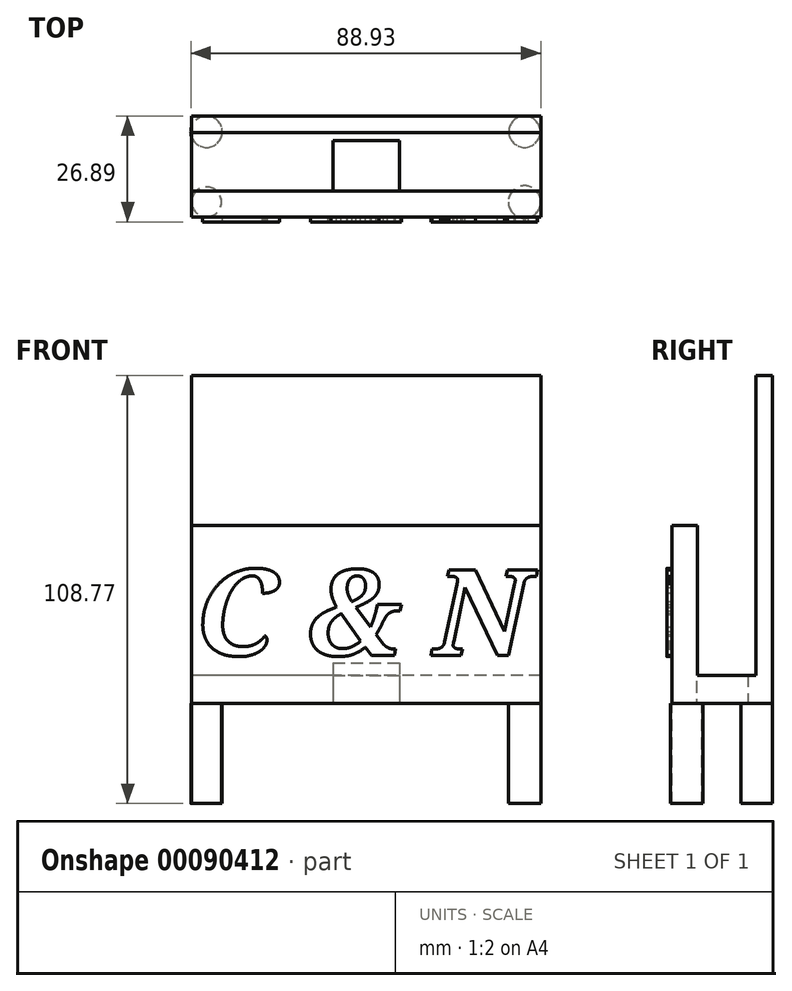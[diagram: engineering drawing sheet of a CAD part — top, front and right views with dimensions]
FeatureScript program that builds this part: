
annotation { "Feature Type Name" : "Feature", "Feature Type Description" : "" }
export const myFeature = defineFeature(function(context is Context, id is Id, definition is map)
    precondition{}
    {
        {
            var Q0;
            Q0=qCreatedBy(makeId("Top.planeOp"),FACE);
            var sketch = newSketch(context, id + "F0", { "sketchPlane" : qUnion([Q0])});
            skLineSegment(sketch, "E0.bottom", {"start": v(44.35, -12.8) * mm, "end": v(-44.35, -12.8) * mm});
            skLineSegment(sketch, "E0.top", {"start": v(44.35, 12.8) * mm, "end": v(-44.35, 12.8) * mm});
            skLineSegment(sketch, "E0.left", {"start": v(44.35, -12.8) * mm, "end": v(44.35, 12.8) * mm});
            skLineSegment(sketch, "E0.right", {"start": v(-44.35, -12.8) * mm, "end": v(-44.35, 12.8) * mm});
            skPoint(sketch, "E0.middle", {"position": v(0, 0) * mm});
            skSolve(sketch);
        }
        {
            var Q0;
            Q0 = qSketchRegion(id + "F0", true);
            extrude(context, id + "F1", {"entities" : qUnion([Q0]), "depth" : 7.17 * mm});
        }
        {
            var Q0;
            Q0=makeQuery(id+"F1.opExtrude","CAP_FACE",FACE,{"disambiguationData":[OSD([sQuery(id+"F0.wireOp",EDGE,"E0.bottom"),sQuery(id+"F0.wireOp",EDGE,"E0.top"),sQuery(id+"F0.wireOp",EDGE,"E0.left"),sQuery(id+"F0.wireOp",EDGE,"E0.right")])],"isStart":false});
            var sketch = newSketch(context, id + "F2", { "sketchPlane" : qUnion([Q0])});
            skLineSegment(sketch, "E1.bottom", {"start": v(44.35, 12.8) * mm, "end": v(-44.35, 12.8) * mm});
            skLineSegment(sketch, "E1.top", {"start": v(44.35, 8.56) * mm, "end": v(-44.35, 8.56) * mm});
            skLineSegment(sketch, "E1.left", {"start": v(44.35, 12.8) * mm, "end": v(44.35, 8.56) * mm});
            skLineSegment(sketch, "E1.right", {"start": v(-44.35, 12.8) * mm, "end": v(-44.35, 8.56) * mm});
            skSolve(sketch);
        }
        {
            var Q0;
            Q0=makeQuery(id+"F2.imprint","IMPRINT",FACE,{"disambiguationData":[TD([[makeQuery(id+"F2.imprint","IMPRINT",EDGE,{"derivedFrom":sQuery(id+"F2.wireOp",EDGE,"E1.bottom")}),1.0]])]});
            extrude(context, id + "F3", {"entities" : qUnion([Q0]), "operationType" : NewBodyOperationType.ADD, "depth" : 76.2 * mm});
        }
        {
            var Q0;
            Q0=makeQuery(id+"F1.opExtrude","CAP_FACE",FACE,{"disambiguationData":[OSD([sQuery(id+"F0.wireOp",EDGE,"E0.bottom"),sQuery(id+"F0.wireOp",EDGE,"E0.top"),sQuery(id+"F0.wireOp",EDGE,"E0.left"),sQuery(id+"F0.wireOp",EDGE,"E0.right")])],"isStart":false});
            var sketch = newSketch(context, id + "F4", { "sketchPlane" : qUnion([Q0])});
            skLineSegment(sketch, "E2.bottom", {"start": v(44.35, -12.8) * mm, "end": v(-44.35, -12.8) * mm});
            skLineSegment(sketch, "E2.top", {"start": v(44.35, -6.26) * mm, "end": v(-44.35, -6.26) * mm});
            skLineSegment(sketch, "E2.left", {"start": v(44.35, -12.8) * mm, "end": v(44.35, -6.26) * mm});
            skLineSegment(sketch, "E2.right", {"start": v(-44.35, -12.8) * mm, "end": v(-44.35, -6.26) * mm});
            skSolve(sketch);
        }
        {
            var Q0;
            Q0 = qSketchRegion(id + "F4", true);
            extrude(context, id + "F5", {"entities" : qUnion([Q0]), "operationType" : NewBodyOperationType.ADD, "depth" : 38.1 * mm});
        }
        {
            var Q0;
            Q0=makeQuery(id+"F1.opExtrude","CAP_FACE",FACE,{"disambiguationData":[OSD([sQuery(id+"F0.wireOp",EDGE,"E0.bottom"),sQuery(id+"F0.wireOp",EDGE,"E0.top"),sQuery(id+"F0.wireOp",EDGE,"E0.left"),sQuery(id+"F0.wireOp",EDGE,"E0.right")])],"isStart":true});
            var sketch = newSketch(context, id + "F6", { "sketchPlane" : qUnion([Q0])});
            skLineSegment(sketch, "E3.bottom", {"start": v(8.42, 6.55) * mm, "end": v(-8.42, 6.55) * mm});
            skLineSegment(sketch, "E3.top", {"start": v(8.42, -6.55) * mm, "end": v(-8.42, -6.55) * mm});
            skLineSegment(sketch, "E3.left", {"start": v(8.42, 6.55) * mm, "end": v(8.42, -6.55) * mm});
            skLineSegment(sketch, "E3.right", {"start": v(-8.42, 6.55) * mm, "end": v(-8.42, -6.55) * mm});
            skPoint(sketch, "E3.middle", {"position": v(0, 0) * mm});
            skSolve(sketch);
        }
        {
            var Q0;
            Q0 = qSketchRegion(id + "F6", true);
            extrude(context, id + "F7", {"entities" : qUnion([Q0]), "operationType" : NewBodyOperationType.REMOVE, "oppositeDirection" : true, "depth" : 10.35 * mm});
        }
        {
            var Q0;
            Q0=makeQuery(id+"F1.opExtrude","CAP_FACE",FACE,{"disambiguationData":[OSD([sQuery(id+"F0.wireOp",EDGE,"E0.bottom"),sQuery(id+"F0.wireOp",EDGE,"E0.top"),sQuery(id+"F0.wireOp",EDGE,"E0.left"),sQuery(id+"F0.wireOp",EDGE,"E0.right")])],"isStart":true});
            var sketch = newSketch(context, id + "F8", { "sketchPlane" : qUnion([Q0])});
            skCircle(sketch, "E4", {"center": v(40.22, 9.01) * mm, "radius": 4.13 * mm});
            skCircle(sketch, "E5", {"center": v(40.22, -8.81) * mm, "radius": 4 * mm});
            skCircle(sketch, "E6", {"center": v(-40.58, -8.81) * mm, "radius": 4 * mm});
            skCircle(sketch, "E7", {"center": v(-40.58, 9.01) * mm, "radius": 3.8 * mm});
            skSolve(sketch);
        }
        {
            var Q0;
            Q0 = qSketchRegion(id + "F8", true);
            extrude(context, id + "F9", {"entities" : qUnion([Q0]), "operationType" : NewBodyOperationType.ADD, "depth" : 25.4 * mm});
        }
        {
            var Q0;
            Q0=makeQuery(id+"F5.boolean.opBoolean","MERGE",FACE,{"derivedFrom":[makeQuery(id+"F1.opExtrude","SWEPT_FACE",FACE,{"disambiguationData":[OSD([sQuery(id+"F0.wireOp",EDGE,"E0.bottom")])]}),makeQuery(id+"F5.opExtrude","SWEPT_FACE",FACE,{"disambiguationData":[OSD([sQuery(id+"F4.wireOp",EDGE,"E2.bottom")])]})]});
            var sketch = newSketch(context, id + "F10", { "sketchPlane" : qUnion([Q0])});
            skText(sketch, "E8", { "text": "C & N", "fontName": "NotoSerif-BoldItalic.ttf"});
            const initialGuessF10  = {"E8": [-0.04345, 0.0122, 1, 0, 0.02192]};
            skSetInitialGuess(sketch, initialGuessF10);
            skSolve(sketch);
        }
        {
            var Q0;
            Q0 = qSketchRegion(id + "F10", true);
            extrude(context, id + "F11", {"entities" : qUnion([Q0]), "operationType" : NewBodyOperationType.ADD, "depth" : 1.27 * mm});
        }
    });
